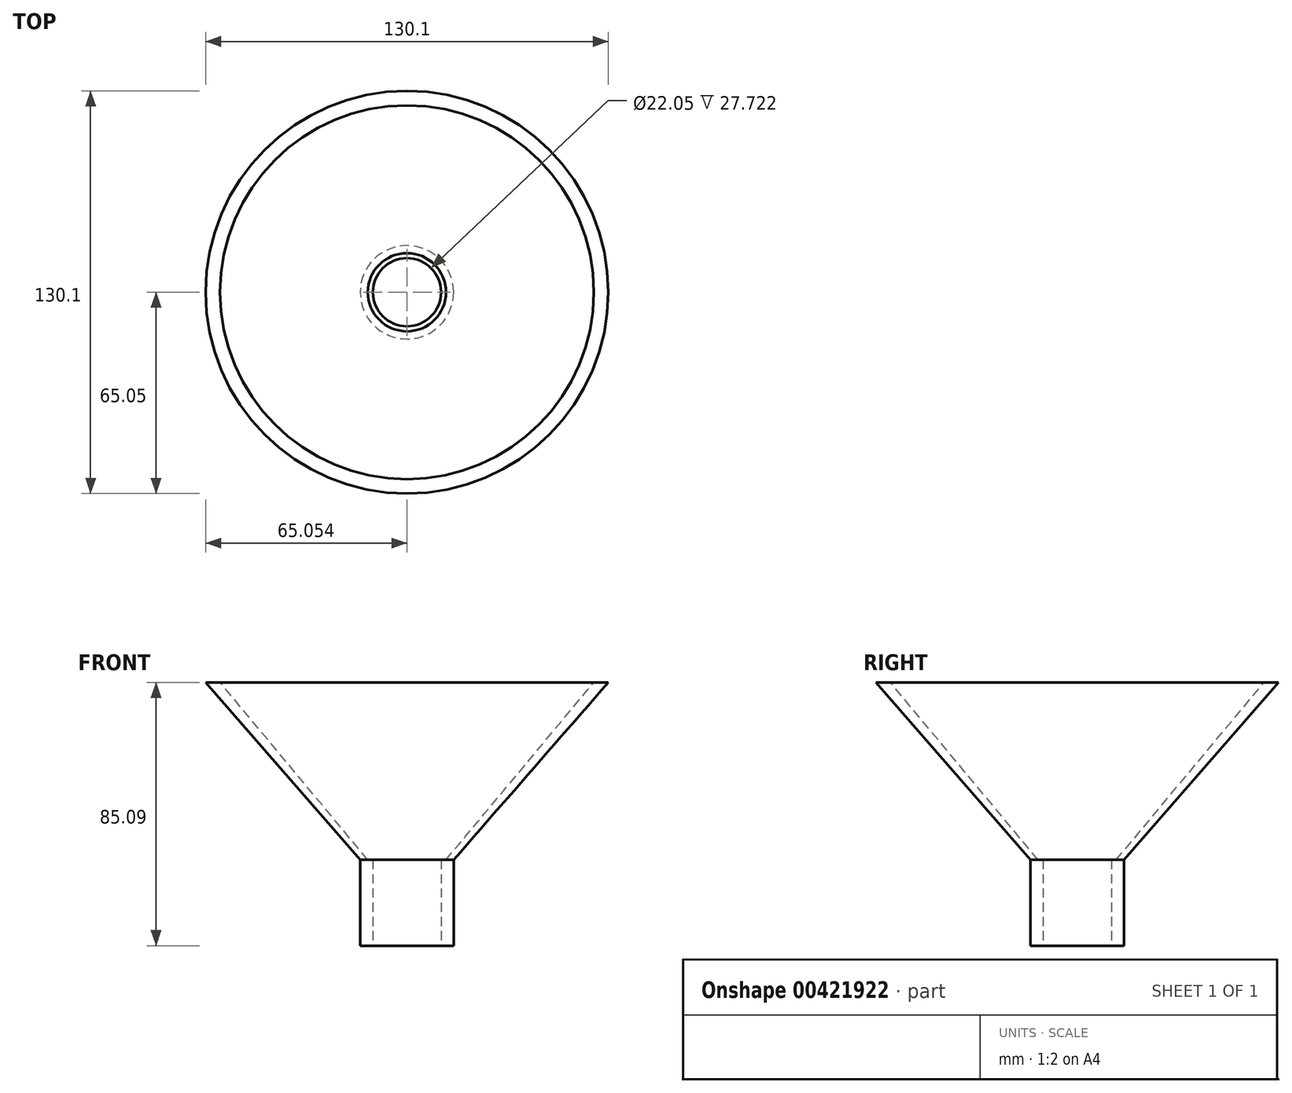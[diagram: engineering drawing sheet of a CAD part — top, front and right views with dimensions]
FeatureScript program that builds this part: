
annotation { "Feature Type Name" : "Feature", "Feature Type Description" : "" }
export const myFeature = defineFeature(function(context is Context, id is Id, definition is map)
    precondition{}
    {
        {
            var Q0;
            Q0=qCreatedBy(makeId("Front.planeOp"),FACE);
            var sketch = newSketch(context, id + "F0", { "sketchPlane" : qUnion([Q0])});
            skLineSegment(sketch, "E0", {"start": v(-15.1, 8.65) * mm, "end": v(-15.1, -19.08) * mm});
            skLineSegment(sketch, "E1", {"start": v(-15.1, -19.08) * mm, "end": v(0, -19.08) * mm});
            skLineSegment(sketch, "E2", {"start": v(0, -19.08) * mm, "end": v(0, 8.65) * mm});
            skPoint(sketch, "E3.end.orphan", {"position": v(19.21, 8.65) * mm});
            skLineSegment(sketch, "E4", {"start": v(0, 8.65) * mm, "end": v(49.95, 66.01) * mm});
            skLineSegment(sketch, "E5", {"start": v(-15.1, 8.65) * mm, "end": v(-2.47, 8.65) * mm});
            skLineSegment(sketch, "E6", {"start": v(-2.47, 8.65) * mm, "end": v(45.29, 66.01) * mm});
            skLineSegment(sketch, "E7", {"start": v(49.95, 66.01) * mm, "end": v(45.29, 66.01) * mm});
            skSolve(sketch);
        }
        {
            var Q0;
            Q0=makeQuery(id+"F0.imprint","IMPRINT",FACE,{"disambiguationData":[TD([[makeQuery(id+"F0.imprint","IMPRINT",EDGE,{"derivedFrom":sQuery(id+"F0.wireOp",EDGE,"E0")}),1.0]])]});
            var Q1;
            Q1=sQuery(id+"F0.wireOp",EDGE,"E0");
            revolve(context, id + "F1", {"entities" : qUnion([Q0]), "axis" : qUnion([Q1]), "revolveType" : RevolveType.FULL});
        }
        {
            var Q0;
            Q0=makeQuery(id+"F1.opRevolve","SWEPT_FACE",FACE,{"disambiguationData":[OSD([sQuery(id+"F0.wireOp",EDGE,"E1")])]});
            var sketch = newSketch(context, id + "F2", { "sketchPlane" : qUnion([Q0])});
            skCircle(sketch, "E8", {"center": v(-15.1, 0) * mm, "radius": 11.03 * mm});
            skSolve(sketch);
        }
        {
            var Q0;
            Q0 = qSketchRegion(id + "F2", true);
            extrude(context, id + "F3", {"entities" : qUnion([Q0]), "operationType" : NewBodyOperationType.REMOVE, "oppositeDirection" : true, "depth" : 50.8 * mm});
        }
    });
